# Revit family: DB
name_source: partatom
category: Mechanical Equipment
units: mm (PartAtom-declared; Revit-internal decimal feet)

## family parameters
Always vertical = Yes
Cut with Voids When Loaded = No
Part Type = Normal
Room Calculation Point = No
Round Connector Dimension = Use Diameter
Shared = No
Work Plane-Based = No

## types (6) — shared parameters
(B-L)/2 = 0' - 1"
0 = 0' - 0"
1.25 = 0' - 1 1/4"
Manufacturer = Loren Cook Company
Model = DB
ONE EIGTH = 0' - 0 1/8"
T_SQ = 1' - 0"
T_SQ_HALF = 0' - 6"
Type Comments = Duct Blower Internal Belt Drive
URL = www.lorencook.com
ZERO = 0' - 0"

## per-type parameters (varying)
| type | -K/2 | A | A/2 | B | B/2 | C | C/2 | D | E | E/2 | F | F/2 | G | H | K | K/2 | L | M | M/2 |
| DB-8 | -0' - 11 1/2" | 1' - 6 1/8" | 0' - 9 1/16" | 1' - 3 7/16" | 0' - 7 23/32" | 1' - 11" | 0' - 11 1/2" | 0' - 7 7/8" | 0' - 9 1/4" | 0' - 4 5/8" | 1' - 9" | 0' - 10 1/2" | 0' - 9 5/8" | 0' - 3 5/16" | 1' - 11" | 0' - 11 1/2" | 1' - 1 7/16" | 1' - 4 1/8" | 0' - 8 1/16" |
| DB-9 | -1' - 1" | 1' - 9 1/8" | 0' - 10 9/16" | 1' - 6 1/8" | 0' - 9 1/16" | 2' - 1 3/4" | 1' - 0 7/8" | 0' - 10 5/16" | 0' - 11 7/8" | 0' - 5 15/16" | 2' - 0" | 1' - 0" | 0' - 11 3/4" | 0' - 3 11/16" | 2' - 2" | 1' - 1" | 1' - 4 1/8" | 1' - 7 1/8" | 0' - 9 9/16" |
| DB-10 | -1' - 2" | 1' - 10 3/8" | 0' - 11 3/16" | 1' - 8 1/8" | 0' - 10 1/16" | 2' - 4 1/4" | 1' - 2 1/8" | 0' - 11 3/8" | 1' - 1 1/8" | 0' - 6 9/16" | 2' - 2" | 1' - 1" | 1' - 1 3/8" | 0' - 3 11/16" | 2' - 4" | 1' - 2" | 1' - 6 1/8" | 1' - 8 3/8" | 0' - 10 3/16" |
| DB-13 | -1' - 4" | 2' - 3 1/8" | 1' - 1 9/16" | 1' - 11 3/16" | 0' - 11 19/32" | 2' - 7 1/4" | 1' - 3 5/8" | 1' - 1 7/16" | 1' - 3 5/8" | 0' - 7 13/16" | 2' - 6" | 1' - 3" | 1' - 4 1/8" | 0' - 3 11/16" | 2' - 8" | 1' - 4" | 1' - 9 3/16" | 2' - 1 1/8" | 1' - 0 9/16" |
| DB-15 | -1' - 7" | 2' - 8 1/2" | 1' - 4 1/4" | 2' - 2 15/16" | 1' - 1 15/32" | 3' - 0 1/4" | 1' - 6 1/8" | 1' - 3 7/8" | 1' - 6 5/8" | 0' - 9 5/16" | 3' - 0" | 1' - 6" | 1' - 7 1/2" | 0' - 3 11/16" | 3' - 2" | 1' - 7" | 2' - 0 15/16" | 2' - 6 1/2" | 1' - 3 1/4" |
| DB-18 | -1' - 11" | 3' - 5" | 1' - 8 1/2" | 2' - 7 7/8" | 1' - 3 15/16" | 3' - 8 3/4" | 1' - 10 3/8" | 1' - 6 7/8" | 1' - 9 7/8" | 0' - 10 15/16" | 3' - 8" | 1' - 10" | 2' - 0" | 0' - 3 7/8" | 3' - 10" | 1' - 11" | 2' - 5 7/8" | 3' - 3" | 1' - 7 1/2" |

## geometry (parser evidence)
native form markers: Sweep x2
no freeform markers — native parametric forms only
